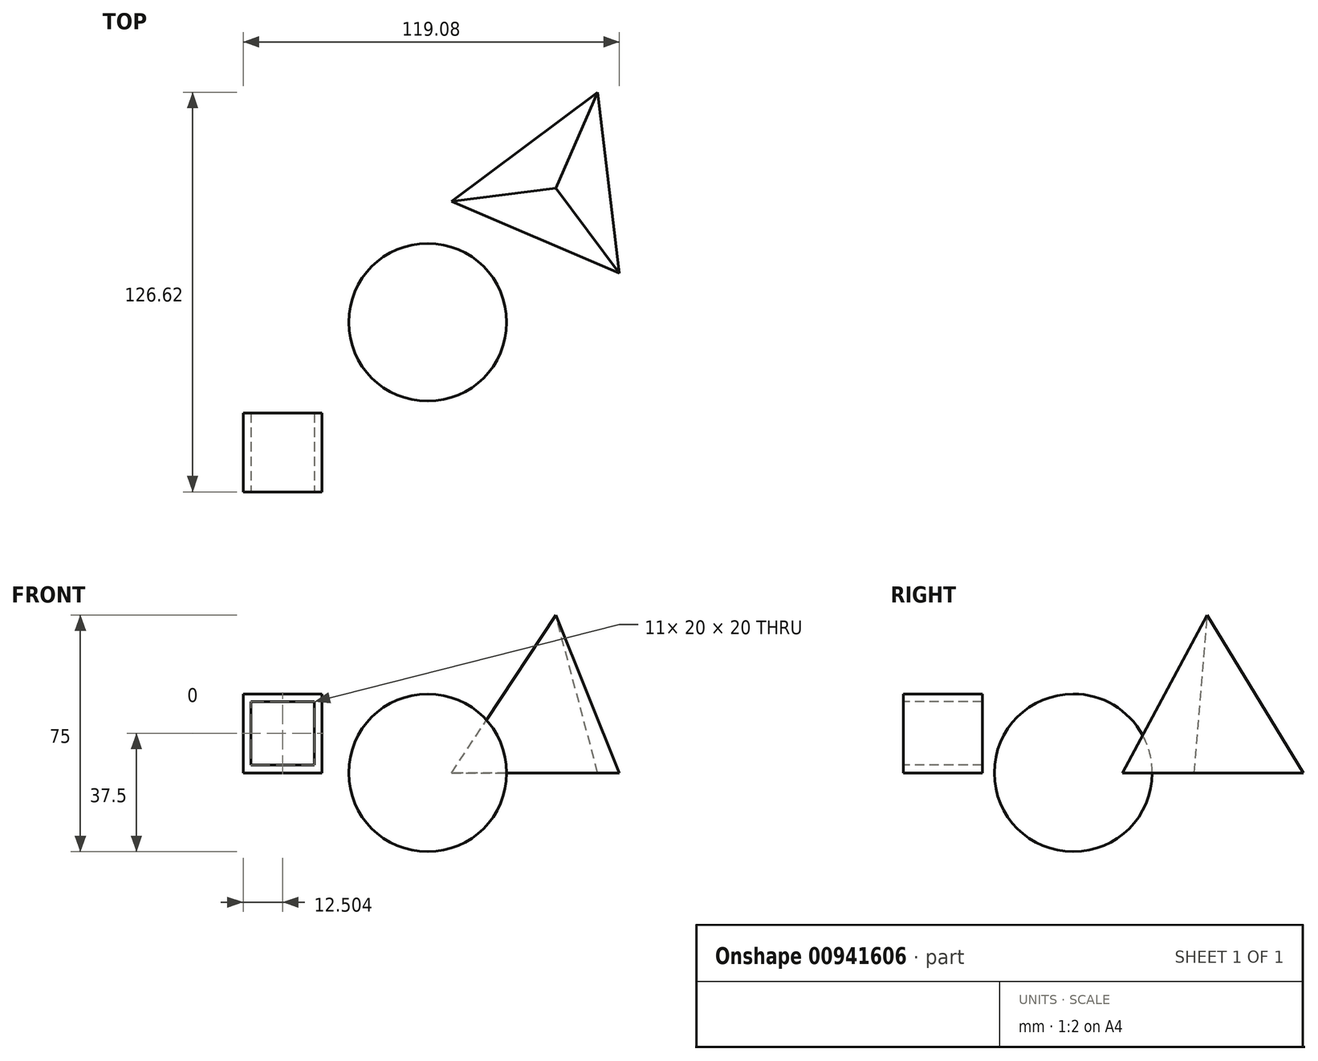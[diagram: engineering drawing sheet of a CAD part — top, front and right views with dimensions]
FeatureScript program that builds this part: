
annotation { "Feature Type Name" : "Feature", "Feature Type Description" : "" }
export const myFeature = defineFeature(function(context is Context, id is Id, definition is map)
    precondition{}
    {
        {
            var Q0;
            Q0=qCreatedBy(makeId("Front.planeOp"),FACE);
            var sketch = newSketch(context, id + "F0", { "sketchPlane" : qUnion([Q0])});
            skArc(sketch, "E0", {"start": v(0, -25) * mm, "mid": v(25, 0) * mm, "end": v(0, 25) * mm});
            skLineSegment(sketch, "E1", {"start": v(0, 25) * mm, "end": v(0, -25) * mm});
            skSolve(sketch);
        }
        {
            var Q0;
            Q0=makeQuery(id+"F0.imprint","IMPRINT",FACE,{"disambiguationData":[TD([[makeQuery(id+"F0.imprint","IMPRINT",EDGE,{"derivedFrom":sQuery(id+"F0.wireOp",EDGE,"E0")}),1.0]])]});
            var Q1;
            Q1=sQuery(id+"F0.wireOp",EDGE,"E1");
            revolve(context, id + "F1", {"surfaceOperationType" : NewSurfaceOperationType.NEW, "entities" : qUnion([Q0]), "axis" : qUnion([Q1]), "revolveType" : RevolveType.FULL});
        }
        {
            var Q0;
            Q0=qCreatedBy(makeId("Top.planeOp"),FACE);
            var sketch = newSketch(context, id + "F2", { "sketchPlane" : qUnion([Q0])});
            skCircle(sketch, "E2.cCircle", {"center": v(40.69, 42.23) * mm, "radius": 16.67 * mm, "construction": true});
            skLineSegment(sketch, "E2.0", {"start": v(53.81, 72.87) * mm, "end": v(60.66, 15.54) * mm});
            skLineSegment(sketch, "E2.1", {"start": v(60.66, 15.54) * mm, "end": v(7.59, 38.27) * mm});
            skLineSegment(sketch, "E2.2", {"start": v(7.59, 38.27) * mm, "end": v(53.81, 72.87) * mm});
            skPoint(sketch, "E2.0.midPoint", {"position": v(57.23, 44.2) * mm});
            skSolve(sketch);
        }
        {
            var Q0;
            Q0=makeQuery(id+"F2.imprint","IMPRINT",FACE,{"disambiguationData":[TD([[makeQuery(id+"F2.imprint","IMPRINT",EDGE,{"derivedFrom":sQuery(id+"F2.wireOp",EDGE,"E2.0")}),-1.0]])]});
            cPlane(context, id + "F3", {"entities" : qUnion([Q0]), "cplaneType" : CPlaneType.OFFSET, "offset" : 50 * mm, "width" : 150 * mm, "height" : 150 * mm});
        }
        {
            var Q0;
            Q0=qCreatedBy(id+"F3.planeOp",FACE);
            var sketch = newSketch(context, id + "F4", { "sketchPlane" : qUnion([Q0])});
            skPoint(sketch, "E3", {"position": v(40.52, 42.42) * mm});
            skSolve(sketch);
        }
        {
            var Q0;
            Q0=makeQuery(id+"F2.imprint","IMPRINT",FACE,{"disambiguationData":[TD([[makeQuery(id+"F2.imprint","IMPRINT",EDGE,{"derivedFrom":sQuery(id+"F2.wireOp",EDGE,"E2.0")}),-1.0]])]});
            var Q1;
            Q1=sQuery(id+"F4.wireOp",VERTEX,"E3");
            loft(context, id + "F5", {"sheetProfilesArray" : [{ "sheetProfileEntities" : qUnion([Q0]) }, { "sheetProfileEntities" : qUnion([Q1]) }]});
        }
        {
            var Q0;
            Q0=qCreatedBy(makeId("Top.planeOp"),FACE);
            var sketch = newSketch(context, id + "F6", { "sketchPlane" : qUnion([Q0])});
            skLineSegment(sketch, "E4.bottom", {"start": v(-58.42, -28.75) * mm, "end": v(-33.42, -28.75) * mm});
            skLineSegment(sketch, "E4.top", {"start": v(-58.42, -53.75) * mm, "end": v(-33.42, -53.75) * mm});
            skLineSegment(sketch, "E4.left", {"start": v(-58.42, -28.75) * mm, "end": v(-58.42, -53.75) * mm});
            skLineSegment(sketch, "E4.right", {"start": v(-33.42, -28.75) * mm, "end": v(-33.42, -53.75) * mm});
            skSolve(sketch);
        }
        {
            var Q0;
            Q0=makeQuery(id+"F6.imprint","IMPRINT",FACE,{"disambiguationData":[TD([[makeQuery(id+"F6.imprint","IMPRINT",EDGE,{"derivedFrom":sQuery(id+"F6.wireOp",EDGE,"E4.bottom")}),-1.0]])]});
            extrude(context, id + "F7", {"entities" : qUnion([Q0]), "depth" : 25 * mm, "offsetDistance" : 25 * mm});
        }
        {
            var Q0;
            Q0=makeQuery(id+"F7.opExtrude","SWEPT_FACE",FACE,{"disambiguationData":[OSD([sQuery(id+"F6.wireOp",EDGE,"E4.top")])]});
            var Q1;
            Q1=makeQuery(id+"F7.opExtrude","SWEPT_FACE",FACE,{"disambiguationData":[OSD([sQuery(id+"F6.wireOp",EDGE,"E4.bottom")])]});
            shell(context, id + "F8", {"entities" : qUnion([Q0, Q1]), "thickness" : 2.5 * mm});
        }
    });
